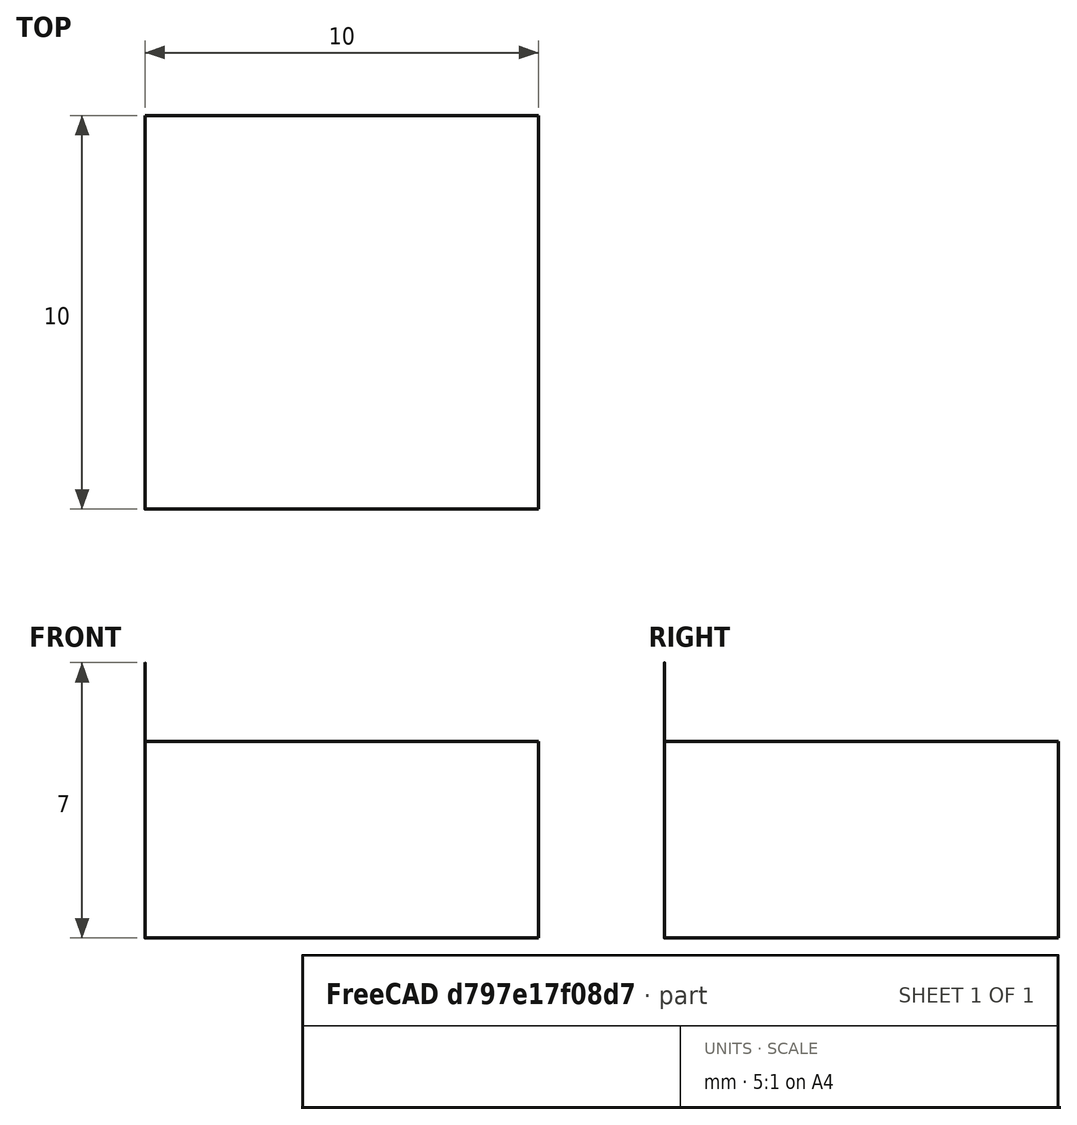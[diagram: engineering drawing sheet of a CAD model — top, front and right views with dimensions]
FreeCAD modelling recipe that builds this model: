
FCSTD DOCUMENT  (FreeCAD 1.0R39109 (Git))
Label: BoxWith9CylinderPockets
License: All rights reserved
LicenseURL: https://en.wikipedia.org/wiki/All_rights_reserved
objects: Part::Cylinder×9, Part::Cut×9, Part::FeaturePython×3, App::DocumentObjectGroup×3, Path::FeaturePython×3, Part::Box×1, App::FeaturePython×1
note: 23 computed .brp shape members not serialized (recipe doc carries the construction recipe); baked Part::Feature solids carry a one-line shape summary decoded from their .brp

FEATURE [Part::Box] Box
  AttacherType = Attacher::AttachEngine3D
  Height = 5
  Length = 10
  Width = 10
FEATURE [Part::Cylinder] Pocket_0_0
  Angle = 360
  AttacherType = Attacher::AttachEngine3D
  FirstAngle = 0
  Height = 0.05
  Placement = pos=(2.375,2.375,4.95) rot=(0,0,1;0rad)
  Radius = 0.25
  SecondAngle = 0
FEATURE [Part::Cylinder] Pocket_0_1
  Angle = 360
  AttacherType = Attacher::AttachEngine3D
  FirstAngle = 0
  Height = 0.05
  Placement = pos=(5,2.375,4.95) rot=(0,0,1;0rad)
  Radius = 0.25
  SecondAngle = 0
FEATURE [Part::Cylinder] Pocket_0_2
  Angle = 360
  AttacherType = Attacher::AttachEngine3D
  FirstAngle = 0
  Height = 0.05
  Placement = pos=(7.625,2.375,4.95) rot=(0,0,1;0rad)
  Radius = 0.25
  SecondAngle = 0
FEATURE [Part::Cylinder] Pocket_1_0
  Angle = 360
  AttacherType = Attacher::AttachEngine3D
  FirstAngle = 0
  Height = 0.05
  Placement = pos=(2.375,5,4.95) rot=(0,0,1;0rad)
  Radius = 0.25
  SecondAngle = 0
FEATURE [Part::Cylinder] Pocket_1_1
  Angle = 360
  AttacherType = Attacher::AttachEngine3D
  FirstAngle = 0
  Height = 0.05
  Placement = pos=(5,5,4.95) rot=(0,0,1;0rad)
  Radius = 0.25
  SecondAngle = 0
FEATURE [Part::Cylinder] Pocket_1_2
  Angle = 360
  AttacherType = Attacher::AttachEngine3D
  FirstAngle = 0
  Height = 0.05
  Placement = pos=(7.625,5,4.95) rot=(0,0,1;0rad)
  Radius = 0.25
  SecondAngle = 0
FEATURE [Part::Cylinder] Pocket_2_0
  Angle = 360
  AttacherType = Attacher::AttachEngine3D
  FirstAngle = 0
  Height = 0.05
  Placement = pos=(2.375,7.625,4.95) rot=(0,0,1;0rad)
  Radius = 0.25
  SecondAngle = 0
FEATURE [Part::Cylinder] Pocket_2_1
  Angle = 360
  AttacherType = Attacher::AttachEngine3D
  FirstAngle = 0
  Height = 0.05
  Placement = pos=(5,7.625,4.95) rot=(0,0,1;0rad)
  Radius = 0.25
  SecondAngle = 0
FEATURE [Part::Cylinder] Pocket_2_2
  Angle = 360
  AttacherType = Attacher::AttachEngine3D
  FirstAngle = 0
  Height = 0.05
  Placement = pos=(7.625,7.625,4.95) rot=(0,0,1;0rad)
  Radius = 0.25
  SecondAngle = 0
FEATURE [Part::Cut] Cut  label="Cut_0"
  Base = -> Box
  Refine = true
  Tool = -> Pocket_0_0
FEATURE [Part::Cut] Cut001  label="Cut_1"
  Base = -> Cut
  Refine = true
  Tool = -> Pocket_0_1
FEATURE [Part::Cut] Cut002  label="Cut_2"
  Base = -> Cut001
  Refine = true
  Tool = -> Pocket_0_2
FEATURE [Part::Cut] Cut003  label="Cut_3"
  Base = -> Cut002
  Refine = true
  Tool = -> Pocket_1_0
FEATURE [Part::Cut] Cut004  label="Cut_4"
  Base = -> Cut003
  Refine = true
  Tool = -> Pocket_1_1
FEATURE [Part::Cut] Cut005  label="Cut_5"
  Base = -> Cut004
  Refine = true
  Tool = -> Pocket_1_2
FEATURE [Part::Cut] Cut006  label="Cut_6"
  Base = -> Cut005
  Refine = true
  Tool = -> Pocket_2_0
FEATURE [Part::Cut] Cut007  label="Cut_7"
  Base = -> Cut006
  Refine = true
  Tool = -> Pocket_2_1
FEATURE [Part::Cut] Cut008  label="Cut_8"
  Base = -> Cut007
  Refine = true
  Tool = -> Pocket_2_2
FEATURE [App::FeaturePython] SetupSheet  # Path/CAM operation (typed FeaturePython)
  ClearanceHeightExpression = OpStockZMax+SetupSheet.ClearanceHeightOffset
  ClearanceHeightOffset = 5
  CoolantMode = 0
  CoolantModes = None | Flood | Mist
  FinalDepthExpression = OpFinalDepth
  HorizRapid = 0
  SafeHeightExpression = OpStockZMax+SetupSheet.SafeHeightOffset
  SafeHeightOffset = 3
  StartDepthExpression = OpStartDepth
  StepDownExpression = OpToolDiameter
  VertRapid = 0
FEATURE [Part::FeaturePython] Clone  label="Model-Cut_8"  # Draft clone (typed FeaturePython)
  AttacherType = Attacher::AttachEngine3D
  Fuse = false
  Objects = -> [Cut008]
  PathResource = Model
  Scale = (1,1,1)
FEATURE [App::DocumentObjectGroup] Model
  Group = -> [Clone]
FEATURE [Part::FeaturePython] ToolBit  label="Drill"  # Path/CAM toolbit (typed FeaturePython)
  BitPropertyNames = Chipload | Diameter | Flutes | Length | Material | TipAngle
  BitShape = <path>
  Chipload = 0
  Diameter = 0.005
  Flutes = 0
  Length = 7
  Material = 0
  ShapeName = drill
  TipAngle = 119
FEATURE [Path::FeaturePython] TC__Default_Tool  label="TC: Default Tool"  # Path/CAM operation (typed FeaturePython)
  HorizFeed = 0
  HorizRapid = 0
  SpindleDir = 0
  SpindleSpeed = 0
  Tool = -> ToolBit
  ToolNumber = 1
  VertFeed = 0
  VertRapid = 0
  expr: HorizRapid = SetupSheet.HorizRapid
  expr: VertRapid = SetupSheet.VertRapid
FEATURE [App::DocumentObjectGroup] Tools
  Group = -> [TC__Default_Tool]
FEATURE [Part::FeaturePython] Stock  # WARN: FeaturePython — macro-defined, semantics opaque (R4)
  Base = -> Model
  ExtXneg = 0.001
  ExtXpos = 0.001
  ExtYneg = 0.001
  ExtYpos = 0.001
  ExtZneg = 0.001
  ExtZpos = 0.001
  StockType = FromBase
FEATURE [Path::FeaturePython] Pocket_Shape  # Path/CAM operation (typed FeaturePython)
  Active = true
  AreaParams:
    Tolerance = 1e-07
    FitArcs = True
    Simplify = False
    CleanDistance = 0.0
    Accuracy = 0.01
    Unit = 1.0
    MinArcPoints = 4
    MaxArcPoints = 100
    ClipperScale = 10000000.0
    Fill = 0
    Coplanar = 0
    Reorient = True
    Outline = False
    Explode = False
    OpenMode = 0
    Deflection = 0.01
    SubjectFill = 0
    ClipFill = 0
    Offset = 0.0
    ExtraPass = 0
    Stepover = 0.0
    LastStepover = 0.0
    JoinType = 0
    EndType = 0
    MiterLimit = 2.0
    RoundPrecision = 0.0
    PocketMode = 1
    ToolRadius = 0.0025
    PocketExtraOffset = 0.0
    PocketStepover = 0.0025
    PocketLastStepover = 0.0
    FromCenter = True
    Angle = 0.0
    AngleShift = 0.0
    Shift = 0.0
    Thicken = False
    SectionCount = -1
    Stepdown = 1.0
    SectionOffset = 0.0
    SectionTolerance = 1e-06
    SectionMode = 2
    Project = False
  Base = -> [Clone]
  ClearanceHeight = 10.001
  CoolantMode = 0
  CutMode = 0
  CycleTime = Cycletime Error
  ExtensionCorners = true
  ExtensionLengthDefault = 0.0025
  ExtraOffset = 0
  FinalDepth = 4.95
  FinishDepth = 0
  KeepToolDown = false
  MinTravel = false
  OffsetPattern = 0
  OpFinalDepth = 4.95
  OpStartDepth = 5.001
  OpStockZMax = 5.001
  OpStockZMin = -0.001
  OpToolDiameter = 0.005
  PathParams = {'orientation': 1, 'feedrate': 0.0, 'feedrate_v': 0.0, 'verbose': True, 'resume_height': 8.001000000000001, 'retraction': 10.001000000000001, 'return_end': True, 'preamble': False, 'start': Vector (7.745632199999999, 5.215088300000001, 10.001000000000001)}
  PocketLastStepOver = 0
  SafeHeight = 8.001
  SplitArcs = false
  StartAt = 0
  StartDepth = 5.001
  StartPoint = (0,0,0)
  StepDown = 0.005
  StepOver = 50
  ToolController = -> TC__Default_Tool
  UseOutline = false
  UseRestMachining = false
  UseStartPoint = false
  ZigZagAngle = 0
  expr: ClearanceHeight = OpStockZMax + SetupSheet.ClearanceHeightOffset
  expr: ExtensionLengthDefault = OpToolDiameter / 2
  expr: FinalDepth = OpFinalDepth
  expr: SafeHeight = OpStockZMax + SetupSheet.SafeHeightOffset
  expr: StartDepth = OpStartDepth
  expr: StepDown = OpToolDiameter
FEATURE [App::DocumentObjectGroup] Operations
  Group = -> [Pocket_Shape]
FEATURE [Path::FeaturePython] Job  # Path/CAM operation (typed FeaturePython)
  CycleTime = 00:00:00
  Fixtures = G54
  GeometryTolerance = 0.01
  JobType = 0
  Model = -> Model
  Operations = -> Operations
  OrderOutputBy = 0
  PostProcessor = 14
  SetupSheet = -> SetupSheet
  SplitOutput = false
  Stock = -> Stock
  Tools = -> Tools
note: 1 file-system path scrubbed to <path> (originals preserved in the JSON sidecar)
